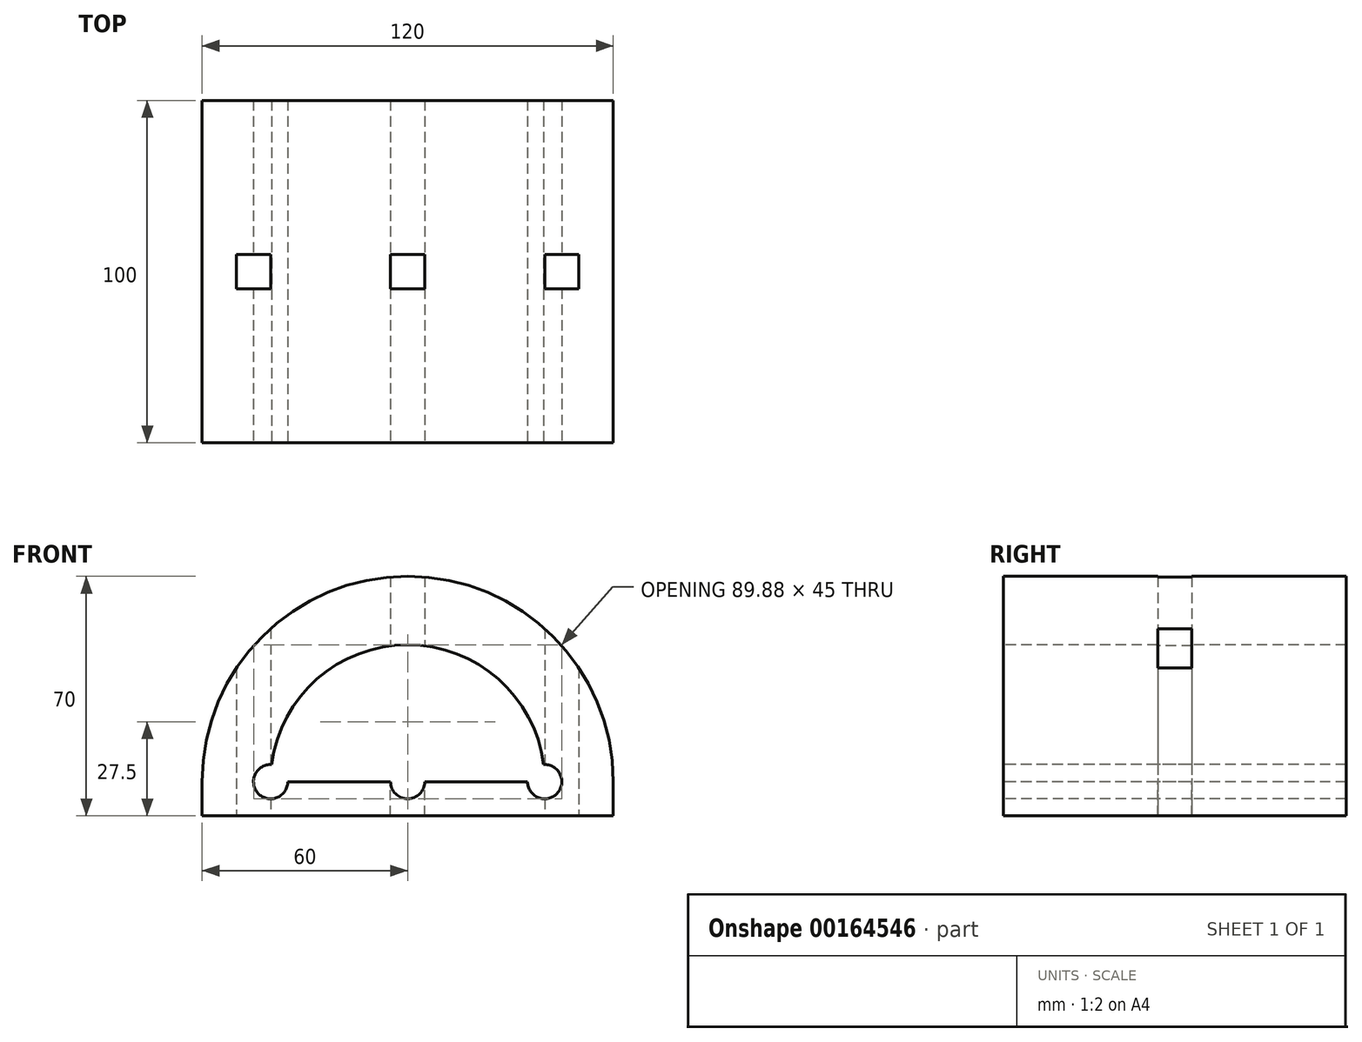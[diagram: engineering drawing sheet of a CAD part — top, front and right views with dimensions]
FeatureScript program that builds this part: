
annotation { "Feature Type Name" : "Feature", "Feature Type Description" : "" }
export const myFeature = defineFeature(function(context is Context, id is Id, definition is map)
    precondition{}
    {
        {
            var Q0;
            Q0=qCreatedBy(makeId("Front.planeOp"),FACE);
            var sketch = newSketch(context, id + "F0", { "sketchPlane" : qUnion([Q0])});
            skArc(sketch, "E0", {"start": v(60, 0) * mm, "mid": v(0, 60) * mm, "end": v(-60, 0) * mm});
            skLineSegment(sketch, "E1", {"start": v(-60, 0) * mm, "end": v(-60, -10) * mm});
            skLineSegment(sketch, "E2", {"start": v(60, 0) * mm, "end": v(60, -10) * mm});
            skLineSegment(sketch, "E3", {"start": v(-60, -10) * mm, "end": v(60, -10) * mm});
            skSolve(sketch);
        }
        {
            var Q0;
            Q0 = qSketchRegion(id + "F0", true);
            extrude(context, id + "F1", {"entities" : qUnion([Q0]), "depth" : 100 * mm});
        }
        {
            var Q0;
            Q0=makeQuery(id+"F1.opExtrude","CAP_FACE",FACE,{"disambiguationData":[OSD([sQuery(id+"F0.wireOp",EDGE,"E0"),sQuery(id+"F0.wireOp",EDGE,"E1"),sQuery(id+"F0.wireOp",EDGE,"E2"),sQuery(id+"F0.wireOp",EDGE,"E3")])],"isStart":false});
            var sketch = newSketch(context, id + "F2", { "sketchPlane" : qUnion([Q0])});
            skArc(sketch, "E4", {"start": v(40, 0) * mm, "mid": v(0, 40) * mm, "end": v(-40, 0) * mm});
            skLineSegment(sketch, "E5", {"start": v(-40, 0) * mm, "end": v(40, 0) * mm});
            skCircle(sketch, "E6", {"center": v(40, 0) * mm, "radius": 5 * mm});
            skCircle(sketch, "E7", {"center": v(0, 0) * mm, "radius": 5 * mm});
            skCircle(sketch, "E8", {"center": v(-40, 0) * mm, "radius": 5 * mm});
            skSolve(sketch);
        }
        {
            var Q0;
            Q0 = qSketchRegion(id + "F2", true);
            extrude(context, id + "F3", {"entities" : qUnion([Q0]), "operationType" : NewBodyOperationType.REMOVE, "endBound" : BoundingType.THROUGH_ALL, "oppositeDirection" : true, "depth" : 25 * mm});
        }
        {
            var Q0;
            Q0=qCreatedBy(makeId("Top.planeOp"),FACE);
            var sketch = newSketch(context, id + "F4", { "sketchPlane" : qUnion([Q0])});
            skLineSegment(sketch, "E9.bottom", {"start": v(5, -45) * mm, "end": v(-5, -45) * mm});
            skLineSegment(sketch, "E9.top", {"start": v(5, -55) * mm, "end": v(-5, -55) * mm});
            skLineSegment(sketch, "E9.left", {"start": v(5, -45) * mm, "end": v(5, -55) * mm});
            skLineSegment(sketch, "E9.right", {"start": v(-5, -45) * mm, "end": v(-5, -55) * mm});
            skPoint(sketch, "E9.middle", {"position": v(0, -50) * mm});
            skSolve(sketch);
        }
        {
            var Q0;
            Q0 = qSketchRegion(id + "F4", true);
            extrude(context, id + "F5", {"entities" : qUnion([Q0]), "operationType" : NewBodyOperationType.REMOVE, "endBound" : BoundingType.THROUGH_ALL, "oppositeDirection" : true, "depth" : 25 * mm});
        }
        {
            var Q0;
            Q0 = qSketchRegion(id + "F4", true);
            extrude(context, id + "F6", {"entities" : qUnion([Q0]), "operationType" : NewBodyOperationType.REMOVE, "endBound" : BoundingType.THROUGH_ALL, "depth" : 25 * mm});
        }
        {
            var Q0;
            Q0=makeQuery(id+"F1.opExtrude","SWEPT_FACE",FACE,{"disambiguationData":[OSD([sQuery(id+"F0.wireOp",EDGE,"E3")])]});
            var sketch = newSketch(context, id + "F7", { "sketchPlane" : qUnion([Q0])});
            skLineSegment(sketch, "E10.bottom", {"start": v(50, 45) * mm, "end": v(40, 45) * mm});
            skLineSegment(sketch, "E10.top", {"start": v(50, 55) * mm, "end": v(40, 55) * mm});
            skLineSegment(sketch, "E10.left", {"start": v(50, 45) * mm, "end": v(50, 55) * mm});
            skLineSegment(sketch, "E10.right", {"start": v(40, 45) * mm, "end": v(40, 55) * mm});
            skPoint(sketch, "E10.middle", {"position": v(45, 50) * mm});
            skPoint(sketch, "E10.middle.positionSnap0", {"position": v(5, 50) * mm});
            skPoint(sketch, "E10.centerSnap0", {"position": v(5, 50) * mm});
            skSolve(sketch);
        }
        {
            var Q0;
            Q0 = qSketchRegion(id + "F7", true);
            extrude(context, id + "F8", {"entities" : qUnion([Q0]), "operationType" : NewBodyOperationType.REMOVE, "endBound" : BoundingType.THROUGH_ALL, "oppositeDirection" : true, "depth" : 25 * mm});
        }
        {
            var Q0;
            Q0=makeQuery(id+"F1.opExtrude","SWEPT_FACE",FACE,{"disambiguationData":[OSD([sQuery(id+"F0.wireOp",EDGE,"E3")])]});
            var sketch = newSketch(context, id + "F9", { "sketchPlane" : qUnion([Q0])});
            skLineSegment(sketch, "E11.bottom", {"start": v(-40, 45) * mm, "end": v(-50, 45) * mm});
            skLineSegment(sketch, "E11.top", {"start": v(-40, 55) * mm, "end": v(-50, 55) * mm});
            skLineSegment(sketch, "E11.left", {"start": v(-40, 45) * mm, "end": v(-40, 55) * mm});
            skLineSegment(sketch, "E11.right", {"start": v(-50, 45) * mm, "end": v(-50, 55) * mm});
            skPoint(sketch, "E11.middle", {"position": v(-45, 50) * mm});
            skPoint(sketch, "E11.middle.positionSnap0", {"position": v(-5, 50) * mm});
            skPoint(sketch, "E11.centerSnap0", {"position": v(-5, 50) * mm});
            skSolve(sketch);
        }
        {
            var Q0;
            Q0 = qSketchRegion(id + "F9", true);
            extrude(context, id + "F10", {"entities" : qUnion([Q0]), "operationType" : NewBodyOperationType.REMOVE, "endBound" : BoundingType.THROUGH_ALL, "oppositeDirection" : true, "depth" : 25 * mm});
        }
    });
